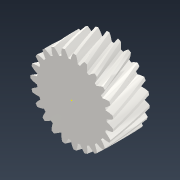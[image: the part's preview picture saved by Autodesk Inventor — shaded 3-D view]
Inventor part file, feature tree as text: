
AUTODESK INVENTOR PART (.ipt)
format: ipt  version: 2022 (Build 260153000, 153)  size: 456,192 bytes
history: native  units: mm (DEFAULTED — no unit token found)
features: plane x3, other x3, sketch x3, extrude x1
ambient origin geometry x8: Origin, YZ Plane, XZ Plane, XY Plane, X Axis, Y Axis, Z Axis, Center Point
bodies: Solid1 (feature_tree)
feature tree (10):
  extrude  "Extrusion1"  Depth=20.0mm TaperAngle=0.0deg
  plane  "Work Plane2"
  plane  "Work Plane8"
  plane  "Work Plane9"
  other  "Spur Gear"
  sketch  "Sketch3"  dims[d4=10.0mm d5=0.0mm d16=104.0mm d17=0.0mm d34=1.570796mm d39=0.0mm d41=0.0mm d43=104.0mm d46=104.0mm d47=0.0mm d48=0.0mm]
  sketch  "Sketch1"  dims[d0=46.170265mm d1=20.0mm d2=0.0mm]
  sketch  "Sketch2"  dims[d3=42.567111mm]
  other  "Srf1"
  other  "Pitch Diameter"
